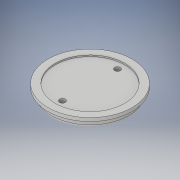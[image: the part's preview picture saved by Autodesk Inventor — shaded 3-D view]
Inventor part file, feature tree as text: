
AUTODESK INVENTOR PART (.ipt)
format: ipt  version: 2017 (Build 210142000, 142)  size: 151,552 bytes
history: native  units: in
note: dims shown in document units (in); Inventor stores cm internally (conversion verified against a paired STEP export)
features: sketch x3, revolve x1, extrude x1, hole x1, fillet x1
ambient origin geometry x8: Origin, YZ Plane, XZ Plane, XY Plane, X Axis, Y Axis, Z Axis, Center Point
bodies: Solid1 (feature_tree)
feature tree (7):
  revolve  "Revolution1"  [1 undecoded]
  extrude  "Extrusion1"  Depth=0.147in
  hole  "Hole3"  [1 undecoded]
  fillet  "Fillet1"  [1 undecoded]
  sketch  "Sketch1"  dims[d0=1.814in d1=0.5in]
  sketch  "Sketch2"  dims[d2=0.691in d3=0.147in]
  sketch  "Sketch5"  dims[d4=1.668in d6=0.195in d10=90.0deg d11=3.0in d12=0.062in d13=0.0in d14=0.939in d15=0.0in d35=2.376in d36=0.25in d37=0.75in d38=0.256in d39=0.134in d40=0.5635in d41=0.3in d42=0.0in d43=0.125in]
note: 3 required parameter values undecoded (feature->parameter linkage not recoverable at this tier; creation-order binding heuristic only, values carry confidence <= 0.55)